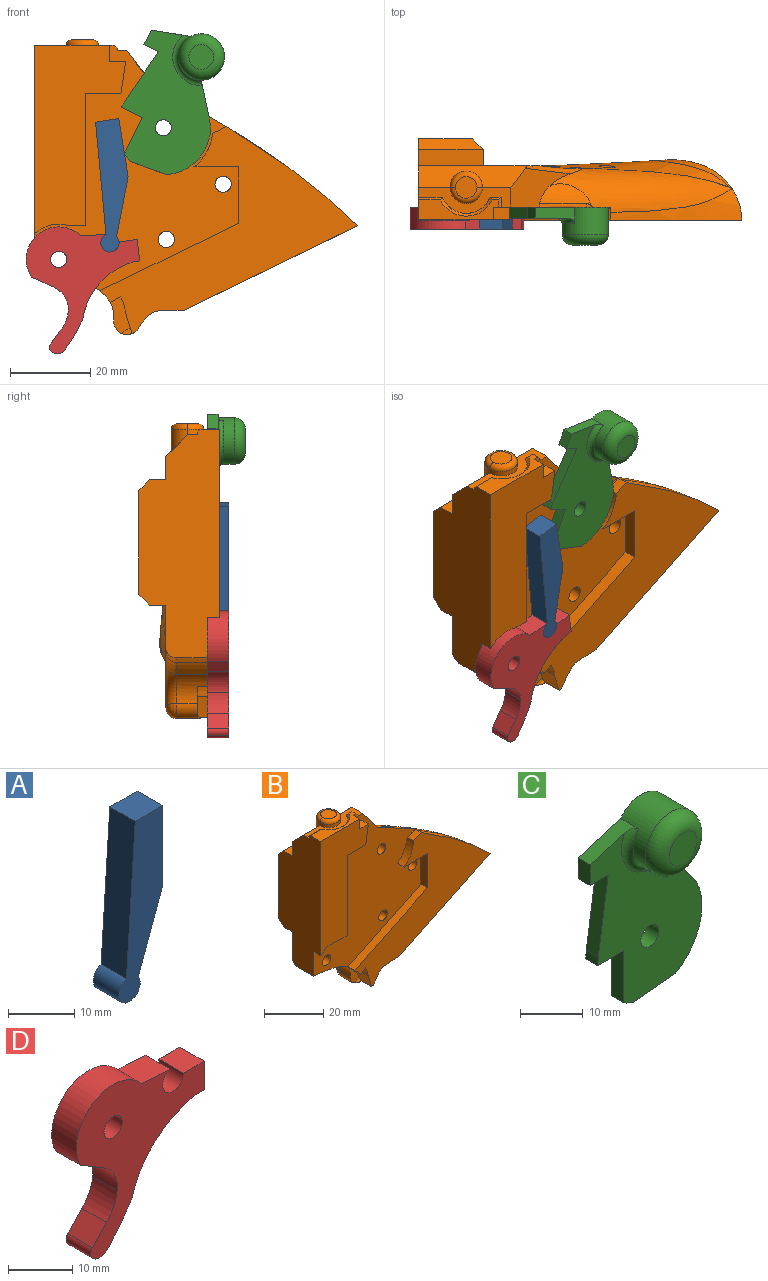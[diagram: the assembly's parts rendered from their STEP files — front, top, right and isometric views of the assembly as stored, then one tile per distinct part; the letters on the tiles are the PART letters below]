
ASSEMBLY  parts=4 mates=3
PART A: 9 faces, bbox 9.4x5.4x32.6 mm
  f0: plane 14.22x5.4mm, normal (0.94,0,-0.34), area 76mm2, adj f1,f4,f5,f6,f8
  f1: cylinder r=2.3mm len=5.4mm, axis (0,1,0), area 62.4mm2, adj f0,f2,f5,f8
  f2: plane 28.08x5.4mm, normal (-1,0,0.07), area 151.9mm2, adj f1,f3,f5,f8
  f3: plane 5.86x5.4mm, normal (0,0,1), area 31.6mm2, adj f2,f4,f5,f8
  f4: plane 14.77x5.4mm, normal (1,0,0), area 79.7mm2, adj f0,f3,f5,f8
  f5: plane 32.58x9.38mm, normal (0,-1,0), area 175.3mm2, adj f0,f1,f2,f3,f4
  f6: cylinder r=1.35mm len=4.73mm, axis (0.94,0,-0.34), area 34.4mm2, adj f0,f7
  f7: plane 2.7x2.54mm, normal (0.94,0,-0.34), area 5.7mm2, adj f6
  f8: plane 32.58x9.38mm, normal (0,1,0), area 175.3mm2, adj f0,f1,f2,f3,f4
PART B: 80 faces, bbox 109.9x29.3x87 mm
  f0: cylinder r=2.02mm len=10.14mm, axis (0,-1,0), area 129.1mm2, adj f45,f79
  f1: cylinder r=2.02mm len=10.44mm, axis (0,-1,0), area 132.8mm2, adj f45,f79
  f2: cylinder r=2.02mm len=9.91mm, axis (0,-1,0), area 126.1mm2, adj f45,f79
  f3: cylinder r=7.71mm len=10.8mm, axis (0,1,0), area 66.2mm2, adj f12,f13,f14,f23,f25,f26,f48,f79
  f4: torus R=2.16mm, axis (0,1,0), area 0mm2, adj f31,f36,f79
  f5: cylinder r=2.02mm len=10.35mm, axis (0,-1,0), area 131.7mm2, adj f50,f73,f79
  f6: plane 5.67x0.24mm, normal (0.46,0,-0.89), area 1.5mm2, adj f7,f12,f13,f14
  f7: cylinder r=10.68mm len=5.67mm, axis (0,1,0), area 22.6mm2, adj f6,f10,f13,f14
  f8: bspline ~28.92x15.16mm, area 75mm2, adj f9,f14,f20,f76
  f9: bspline ~28.92x15.16mm, area 2.6mm2, adj f8,f14,f21,f22
  f10: plane 5.69x5.41mm, normal (-0.96,0,-0.29), area 31.6mm2, adj f7,f11,f13,f14,f23
  f11: torus R=8.99mm, axis (0,-1,0), area 2.8mm2, adj f10,f13,f23
  f12: plane 5.68x2.44mm, normal (0.44,0,-0.9), area 15.3mm2, adj f3,f6,f13,f14
  f13: plane 9.04x5.07mm, normal (0,-1,0), area 26.1mm2, adj f3,f6,f7,f10,f11,f12,f23
  f14: plane 64.58x51.89mm, normal (0,-1,0), area 1073.3mm2, adj f3,f6,f7,f8,f9,f10,f12,f17
  f15: plane 5.47x5.4mm, normal (0,0,1), area 22.9mm2, adj f24,f33
  f16: torus R=2.16mm, axis (0,1,0), area 0mm2, adj f32,f35
  f17: bspline ~76.77x72.19mm, area 151.9mm2, adj f14,f18,f30,f36,f76
  f18: bspline ~0.66x0.64mm, area 0.2mm2, adj f17,f19,f36,f76
  f19: bspline ~55.38x48.21mm, area 90.1mm2, adj f18,f45,f76
  f20: bspline ~12.34x4.81mm, area 41.6mm2, adj f8,f21,f45,f76
  f21: bspline ~29.86x10.46mm, area 1.2mm2, adj f9,f20,f45,f46
  f22: cylinder r=10.09mm len=10.8mm, axis (0,1,0), area 62.4mm2, adj f9,f14,f23,f46
  f23: cylinder r=3.36mm len=10.8mm, axis (0,1,0), area 61.9mm2, adj f3,f10,f11,f13,f14,f22,f47
  f24: torus R=2.7mm, axis (0,0,1), area 23.7mm2, adj f15,f33,f55
  f25: cylinder r=23mm len=7.65mm, axis (0,1,0), area 62.7mm2, adj f3,f37,f49,f79
  f26: plane 34.64x16.8mm, normal (-0.44,0,0.9), area 121.3mm2, adj f3,f14,f27,f79
  f27: plane 14.13x3.15mm, normal (-1,0,0), area 44.5mm2, adj f14,f26,f28,f79
  f28: plane 11.11x3.15mm, normal (0,0,-1), area 35mm2, adj f14,f27,f29,f79
  f29: cylinder r=12.39mm len=8.42mm, axis (0,-1,0), area 31.1mm2, adj f14,f28,f30,f78,f79
  f30: bspline ~4.28x3.47mm, area 11.6mm2, adj f14,f17,f29,f36,f77,f78
  f31: plane 0.43x0.25mm, normal (-0.04,0,1), area 0.1mm2, adj f4,f32,f79
  f32: plane 1.58x1.2mm, normal (0.44,0,0.9), area 1.1mm2, adj f16,f31,f34,f79
  f33: torus R=2.7mm, axis (0,0,1), area 23.7mm2, adj f15,f24,f61
  f34: extruded ~11.63x6.21mm, area 11.9mm2, adj f32,f35,f62,f79
  f35: bspline ~15.1x9.71mm, area 56.8mm2, adj f16,f34,f36,f62
  f36: bspline ~52.78x35.74mm, area 528.9mm2, adj f4,f17,f18,f30,f35,f45,f62,f63
  f37: cylinder r=58.04mm len=8.59mm, axis (0,1,0), area 66.3mm2, adj f25,f50,f75,f79
  f38: cylinder r=8.78mm len=8.62mm, axis (0,-1,0), area 29.2mm2, adj f39,f74,f75,f79
  f39: plane 4.05x3.15mm, normal (0,0,-1), area 12.8mm2, adj f38,f40,f74,f79
  f40: plane 32.99x3.15mm, normal (1,0,0), area 103.9mm2, adj f39,f41,f74,f79
  f41: plane 8.89x3.15mm, normal (0,0,-1), area 28mm2, adj f40,f42,f74,f79
  f42: plane 7.99x3.15mm, normal (0.99,0,-0.15), area 25.5mm2, adj f41,f43,f74,f79
  f43: plane 4.05x3.15mm, normal (0,0,1), area 12.8mm2, adj f42,f56,f74,f79
  f44: plane 16.16x4.05mm, normal (0,0,1), area 65.4mm2, adj f64,f66,f73,f75
  f45: bspline ~60.65x48.21mm, area 1068.1mm2, adj f0,f1,f2,f19,f20,f21,f36,f63
  f46: torus R=12.79mm, axis (0,-1,0), area 29.3mm2, adj f21,f22,f47,f73
  f47: revolved ~6.33x3.69mm, area 27.7mm2, adj f23,f46,f48,f73
  f48: torus R=10.41mm, axis (0,-1,0), area 40.9mm2, adj f3,f47,f49,f73
  f49: torus R=25.7mm, axis (0,-1,0), area 36.3mm2, adj f25,f48,f50,f73
  f50: torus R=60.74mm, axis (0,-1,0), area 36.8mm2, adj f5,f37,f49,f73,f75
  f51: plane 5.88x0.68mm, normal (0,1,0), area 4mm2, adj f52,f60,f72,f75
  f52: cylinder r=6.49mm len=12.02mm, axis (0,0,1), area 10.4mm2, adj f51,f53,f59,f72
  f53: plane 2.7x0.68mm, normal (0,1,0), area 1.8mm2, adj f52,f54,f58,f72
  f54: plane 2.51x0.68mm, normal (1,0,0), area 1.7mm2, adj f53,f57,f72,f79
  f55: cylinder r=4.05mm len=8.1mm, axis (0,0,-1), area 17.2mm2, adj f24,f61,f72
  f56: plane 4.05x3.15mm, normal (1,0,0), area 12.8mm2, adj f43,f70,f74,f79
  f57: plane 2.51x0.68mm, normal (0.71,0,0.71), area 2.1mm2, adj f54,f58,f70,f79
  f58: plane 2.71x0.69mm, normal (0,0.71,0.71), area 2mm2, adj f53,f57,f59,f70
  f59: cone r=6.82mm half-angle=45deg, axis (0,0,1), area 15mm2, adj f52,f58,f60,f70
  f60: plane 5.9x0.69mm, normal (0,0.71,0.71), area 5.4mm2, adj f51,f59,f70,f75
  f61: cylinder r=4.05mm len=8.1mm, axis (0,0,-1), area 50mm2, adj f33,f55,f71
  f62: plane 20.29x15.76mm, normal (0.79,0,0.61), area 132.9mm2, adj f34,f35,f36,f63,f71,f72,f79
  f63: bspline ~24.12x18.82mm, area 39.3mm2, adj f36,f45,f62,f71,f73
  f64: plane 16.16x2.7mm, normal (0,0.71,0.71), area 56.5mm2, adj f44,f65,f69,f75
  f65: plane 31.32x2.7mm, normal (0.71,0.71,0), area 109.3mm2, adj f64,f66,f68,f69
  f66: plane 31.32x4.05mm, normal (1,0,0), area 126.9mm2, adj f44,f65,f67,f73
  f67: plane 16.16x4.05mm, normal (0,0,-1), area 65.4mm2, adj f66,f68,f73,f75
  f68: plane 16.16x2.7mm, normal (0,0.71,-0.71), area 56.5mm2, adj f65,f67,f69,f75
  f69: plane 25.92x13.46mm, normal (0,1,0), area 348.8mm2, adj f64,f65,f68,f75
  f70: plane 19.92x4.99mm, normal (0,0,1), area 58.1mm2, adj f56,f57,f58,f59,f60,f74,f75,f79
  f71: plane 26.99x5.47mm, normal (0,0.71,0.71), area 155.2mm2, adj f61,f62,f63,f72,f73,f75
  f72: plane 23.04x6.56mm, normal (0,0,1), area 71.7mm2, adj f51,f52,f53,f54,f55,f62,f71,f75
  f73: plane 63.12x30.43mm, normal (0,1,0), area 1055.2mm2, adj f5,f44,f45,f46,f47,f48,f49,f50
  f74: plane 47.02x22.74mm, normal (0,-1,0), area 672.2mm2, adj f38,f39,f40,f41,f42,f43,f56,f70
  f75: plane 57.11x20.31mm, normal (-1,0,0), area 915.7mm2, adj f37,f38,f44,f50,f51,f60,f64,f67
  f76: plane 46.34x24.01mm, normal (0.44,0,-0.9), area 594.9mm2, adj f8,f14,f17,f18,f19,f20,f45
  f77: bspline ~1.3x0.61mm, area 0.3mm2, adj f30,f36,f78,f79
  f78: bspline ~2.21x1.04mm, area 0.4mm2, adj f29,f30,f77,f79
  f79: plane 61.28x50.91mm, normal (0,-1,0), area 1601.6mm2, adj f0,f1,f2,f3,f4,f5,f25,f26
PART C: 22 faces, bbox 25.5x9.8x37.8 mm
  f0: plane 6.18x6.18mm, normal (0,-1,0), area 30mm2, adj f1
  f1: torus R=3.09mm, axis (0,-1,0), area 128.1mm2, adj f0,f11
  f2: torus R=7.14mm, axis (0,1,0), area 34.1mm2, adj f4,f10,f11,f12
  f3: cylinder r=2.02mm len=4.05mm, axis (0,1,0), area 34.4mm2, adj f4,f21
  f4: plane 34.02x25.17mm, normal (0,-1,0), area 473.6mm2, adj f2,f3,f7,f8,f9,f10,f12,f13
  f5: plane 2.69x1.35mm, normal (0.1,0,-1), area 2.9mm2, adj f6,f21
  f6: cylinder r=1.35mm len=6.98mm, axis (0.1,0,-1), area 28.6mm2, adj f5,f20,f21
  f7: plane 10.14x2.7mm, normal (-1,0,0), area 27.4mm2, adj f4,f8,f18,f21
  f8: plane 5.86x2.7mm, normal (0,0,-1), area 15.8mm2, adj f4,f7,f17,f21
  f9: cylinder r=11.71mm len=3mm, axis (0,1,0), area 9.4mm2, adj f4,f10,f16,f21
  f10: plane 7.66x6.04mm, normal (0.79,0,0.62), area 26.4mm2, adj f2,f4,f9,f11,f21
  f11: cylinder r=5.79mm len=11.58mm, axis (0,1,0), area 183.3mm2, adj f1,f2,f10,f12,f21
  f12: plane 9.91x4.4mm, normal (-0.29,0,0.96), area 27.6mm2, adj f2,f4,f11,f13,f21
  f13: plane 4.05x2.7mm, normal (-1,0,0), area 10.9mm2, adj f4,f12,f14,f21
  f14: plane 4.05x2.7mm, normal (0,0,-1), area 10.9mm2, adj f4,f13,f15,f21
  f15: plane 14.82x2.7mm, normal (-0.99,0,0.15), area 40.4mm2, adj f4,f14,f17,f21
  f16: extruded ~2.7x1.24mm, area 3.5mm2, adj f4,f9,f19,f21
  f17: cylinder r=11.71mm len=2.7mm, axis (0,1,0), area 4.6mm2, adj f4,f8,f15,f21
  f18: cylinder r=11.71mm len=2.7mm, axis (0,1,0), area 6.4mm2, adj f4,f7,f20,f21
  f19: cylinder r=11.71mm len=13.17mm, axis (0,1,0), area 41.5mm2, adj f4,f16,f20,f21
  f20: plane 9.5x2.7mm, normal (0.1,0,-1), area 22.9mm2, adj f4,f6,f18,f19,f21
  f21: plane 36.93x25.17mm, normal (0,1,0), area 583mm2, adj f3,f5,f6,f7,f8,f9,f10,f11
PART D: 17 faces, bbox 28.1x5.4x31.5 mm
  f0: cylinder r=8.1mm len=14.37mm, axis (0,1,0), area 127.4mm2, adj f7,f9,f10,f16
  f1: cylinder r=50.99mm len=6.96mm, axis (0,1,0), area 47.5mm2, adj f2,f9,f13,f16
  f2: cylinder r=2.24mm len=5.4mm, axis (0,1,0), area 20mm2, adj f1,f3,f9,f16
  f3: cylinder r=1.43mm len=5.4mm, axis (0,1,0), area 11.5mm2, adj f2,f4,f9,f16
  f4: plane 5.4x3.33mm, normal (-0.74,0,0.68), area 24.4mm2, adj f3,f5,f9,f16
  f5: cylinder r=7.92mm len=5.4mm, axis (0,1,0), area 30mm2, adj f4,f6,f9,f16
  f6: cylinder r=5.94mm len=5.7mm, axis (0,1,0), area 36.3mm2, adj f5,f7,f9,f16
  f7: plane 5.4x5.34mm, normal (-0.52,0,-0.85), area 33.7mm2, adj f0,f6,f9,f16
  f8: cylinder r=2.02mm len=5.4mm, axis (0,1,0), area 68.7mm2, adj f9,f16
  f9: plane 31.51x28.13mm, normal (0,-1,0), area 361.9mm2, adj f0,f1,f2,f3,f4,f5,f6,f7
  f10: plane 6.29x5.4mm, normal (0.06,0,1), area 34mm2, adj f0,f9,f11,f16
  f11: cylinder r=2.3mm len=5.4mm, axis (0,1,0), area 54.8mm2, adj f9,f10,f12,f16
  f12: plane 5.4x4.55mm, normal (-0.01,0,1), area 24.6mm2, adj f9,f11,f15,f16
  f13: cylinder r=17.74mm len=14.59mm, axis (0,1,0), area 111.2mm2, adj f1,f9,f14,f16
  f14: plane 5.4x1.35mm, normal (0,0,-1), area 7.3mm2, adj f9,f13,f15,f16
  f15: plane 5.41x5.4mm, normal (1,0,0), area 29.2mm2, adj f9,f12,f14,f16
  f16: plane 31.51x28.13mm, normal (0,1,0), area 361.9mm2, adj f0,f1,f2,f3,f4,f5,f6,f7
PLACE A rot(axis=(0,-1,0),9.1deg) t=(-35.86,56.06,-12.48)mm
PLACE B t=(-40.83,55.61,1.61)mm fixed
PLACE C rot(axis=(0,1,0),26deg) t=(-53.96,58.76,57.49)mm
PLACE D rot(axis=(0,-1,0),6.9deg) t=(-37.35,56.06,-8.88)mm
MATE revolute A.f1 <-> D.f11  axis (0,-1,0) through (60.12,-12.37,29.23)mm
MATE revolute C.f3 <-> B.f29  axis (0,1,0) through (73.47,-6.97,57.94)mm
MATE revolute B.f38 <-> D.f0  axis (0,-1,0) through (47.35,-6.97,25.1)mm
